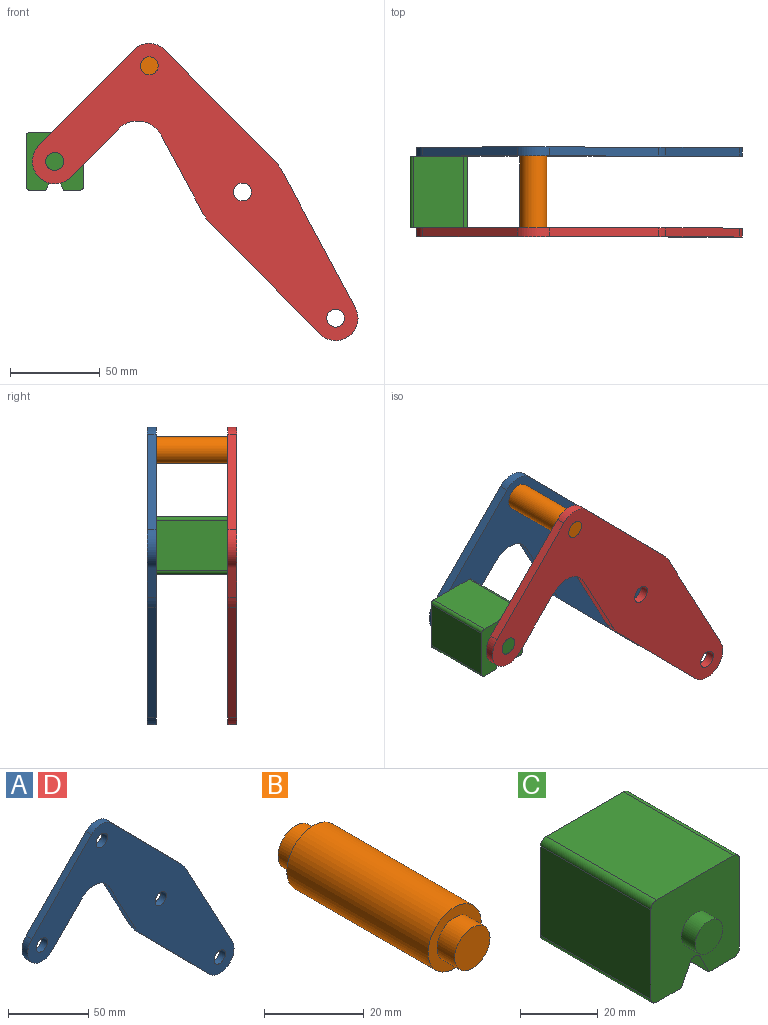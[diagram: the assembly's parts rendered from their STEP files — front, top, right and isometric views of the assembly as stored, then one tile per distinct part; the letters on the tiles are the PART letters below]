
ASSEMBLY  parts=4 mates=1
PART A: 18 faces, bbox 181.7x5x165.8 mm
  f0: plane 43.49x23.35mm, normal (-0.88,0,-0.47), area 246.8mm2, adj f1,f14,f16,f17
  f1: cylinder r=25mm len=5.75mm, axis (0,1,0), area 35.8mm2, adj f0,f2,f16,f17
  f2: plane 61.6x60.87mm, normal (-0.71,0,-0.7), area 433mm2, adj f1,f3,f16,f17
  f3: cylinder r=12.5mm len=21.39mm, axis (0,1,0), area 178.4mm2, adj f2,f4,f16,f17
  f4: plane 76.3x40.96mm, normal (0.88,0,0.47), area 433mm2, adj f3,f5,f16,f17
  f5: cylinder r=25mm len=5.75mm, axis (0,1,0), area 35.8mm2, adj f4,f6,f16,f17
  f6: plane 61.6x60.87mm, normal (0.71,0,0.7), area 433mm2, adj f5,f7,f16,f17
  f7: cylinder r=12.5mm len=17.78mm, axis (0,1,0), area 98.9mm2, adj f6,f8,f16,f17
  f8: plane 53.35x52.71mm, normal (-0.71,0,0.7), area 375mm2, adj f7,f9,f16,f17
  f9: cylinder r=12.5mm len=21.39mm, axis (0,1,0), area 196.3mm2, adj f8,f10,f16,f17
  f10: plane 26.86x26.54mm, normal (0.71,0,-0.7), area 188.8mm2, adj f9,f14,f16,f17
  f11: cylinder r=5mm len=10mm, axis (0,1,0), area 157.1mm2, adj f16,f17
  f12: cylinder r=5mm len=10mm, axis (0,1,0), area 157.1mm2, adj f16,f17
  f13: cylinder r=5mm len=10mm, axis (0,1,0), area 157.1mm2, adj f16,f17
  f14: cylinder r=15mm len=23.89mm, axis (0,1,0), area 140.2mm2, adj f0,f10,f16,f17
  f15: cylinder r=5mm len=10mm, axis (0,1,0), area 157.1mm2, adj f16,f17
  f16: plane 181.66x165.78mm, normal (0,-1,0), area 8710.1mm2, adj f0,f1,f2,f3,f4,f5,f6,f7
  f17: plane 181.66x165.78mm, normal (0,1,0), area 8710.1mm2, adj f0,f1,f2,f3,f4,f5,f6,f7
PART B: 7 faces, bbox 15x50x15 mm
  f0: cylinder r=7.5mm len=40mm, axis (0,-1,0), area 1885mm2, adj f2,f5
  f1: cylinder r=5mm len=10mm, axis (0,1,0), area 157.1mm2, adj f2,f3
  f2: plane 15x15mm, normal (0,-1,0), area 98.2mm2, adj f0,f1
  f3: plane 10x10mm, normal (0,-1,0), area 78.5mm2, adj f1
  f4: cylinder r=5mm len=10mm, axis (0,-1,0), area 157.1mm2, adj f5,f6
  f5: plane 15x15mm, normal (0,1,0), area 98.2mm2, adj f0,f4
  f6: plane 10x10mm, normal (0,1,0), area 78.5mm2, adj f4
PART C: 18 faces, bbox 32.1x50x32.1 mm
  f0: plane 40x28.08mm, normal (1,0,0), area 1123.1mm2, adj f4,f10,f13,f14
  f1: plane 40x9.04mm, normal (0,0,-1), area 361.6mm2, adj f2,f4,f10,f14
  f2: plane 40x6.42mm, normal (-0.89,0,-0.45), area 287.2mm2, adj f1,f4,f10,f15
  f3: plane 40x6.42mm, normal (0.89,0,-0.45), area 287.2mm2, adj f4,f5,f10,f15
  f4: plane 32.08x32.08mm, normal (0,-1,0), area 900.6mm2, adj f0,f1,f2,f3,f5,f6,f7,f9
  f5: plane 40x9.04mm, normal (0,0,-1), area 361.6mm2, adj f3,f4,f10,f16
  f6: plane 40x28.08mm, normal (0,0,1), area 1123.1mm2, adj f4,f10,f13,f17
  f7: plane 40x28.08mm, normal (-1,0,0), area 1123.1mm2, adj f4,f10,f16,f17
  f8: plane 10x10mm, normal (0,-1,0), area 78.5mm2, adj f9
  f9: cylinder r=5mm len=10mm, axis (0,1,0), area 157.1mm2, adj f4,f8
  f10: plane 32.08x32.08mm, normal (0,1,0), area 900.6mm2, adj f0,f1,f2,f3,f5,f6,f7,f12
  f11: plane 10x10mm, normal (0,1,0), area 78.5mm2, adj f12
  f12: cylinder r=5mm len=10mm, axis (0,-1,0), area 157.1mm2, adj f10,f11
  f13: cylinder r=2mm len=40mm, axis (0,1,0), area 125.7mm2, adj f0,f4,f6,f10
  f14: cylinder r=2mm len=40mm, axis (0,-1,0), area 125.7mm2, adj f0,f1,f4,f10
  f15: cylinder r=2mm len=40mm, axis (0,1,0), area 177.1mm2, adj f2,f3,f4,f10
  f16: cylinder r=2mm len=40mm, axis (0,1,0), area 125.7mm2, adj f4,f5,f7,f10
  f17: cylinder r=2mm len=40mm, axis (0,-1,0), area 125.7mm2, adj f4,f6,f7,f10
PART D: same geometry as A
PLACE A t=(0,25,0)mm fixed
PLACE B t=(0,-20,0)mm
PLACE C t=(0,-20,0)mm
PLACE D t=(0,-20,0)mm
MATE revolute C.f9 <-> A.f9  axis (0,-1,0) through (-104.69,20,17.04)mm
